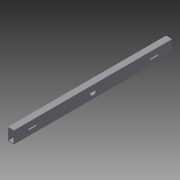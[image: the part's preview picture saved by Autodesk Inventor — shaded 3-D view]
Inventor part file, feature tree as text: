
AUTODESK INVENTOR PART (.ipt)
format: ipt  version: 2015 SP1 (Build 190203100, 203)  size: 123,904 bytes
history: native  units: in
note: dims shown in document units (in); Inventor stores cm internally (conversion verified against a paired STEP export)
features: extrude x2, sketch x2, projected_geometry x1
ambient origin geometry x8: Origin, YZ Plane, XZ Plane, XY Plane, X Axis, Y Axis, Z Axis, Center Point
bodies: Solid1 (feature_tree)
feature tree (5):
  extrude  "Extrusion1"  Depth=2.0in
  extrude  "Extrusion2"  Depth=1.75in
  sketch  "Sketch1"  dims[d0=1.0in d1=2.0in]
  sketch  "Sketch2"  dims[d2=0.75in d3=1.75in d4=0.125in d5=0.125in d6=26.0in d7=0.0in d8=1.0in d9=13.0in d10=1.0in d11=1.0in d12=1.0in d13=1.0in d14=1.0in d15=2.5in d16=2.5in d17=3.5in d18=3.5in d19=0.1875in d20=0.375in d21=0.1875in d22=0.375in d23=0.1875in d24=90.0deg d25=0.375in d26=0.1875in d27=90.0deg d28=0.375in d29=0.1877in d30=0.1892in d31=0.1901in d32=0.1875in d33=30.0in d34=0.0in]
  projected_geometry  "Projected Loop1"
